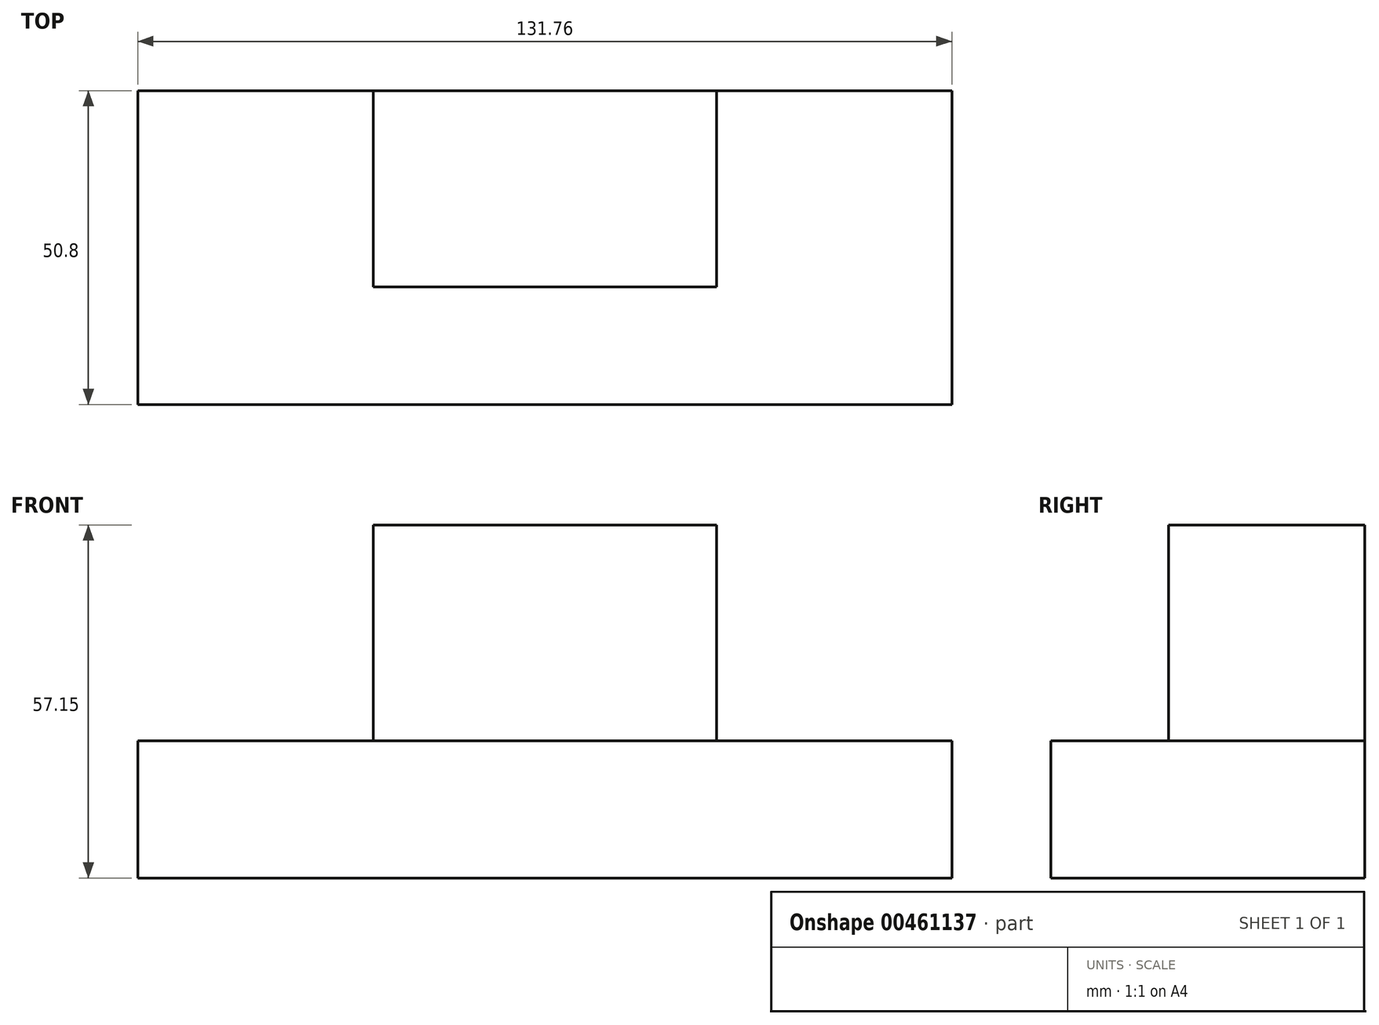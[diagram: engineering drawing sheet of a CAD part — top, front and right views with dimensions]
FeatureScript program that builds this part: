
annotation { "Feature Type Name" : "Feature", "Feature Type Description" : "" }
export const myFeature = defineFeature(function(context is Context, id is Id, definition is map)
    precondition{}
    {
        {
            var Q0;
            Q0=qCreatedBy(makeId("Front.planeOp"),FACE);
            var sketch = newSketch(context, id + "F0", { "sketchPlane" : qUnion([Q0])});
            skLineSegment(sketch, "E0.bottom", {"start": v(0, 0) * mm, "end": v(131.76, 0) * mm});
            skLineSegment(sketch, "E0.top", {"start": v(0, 22.23) * mm, "end": v(131.76, 22.23) * mm});
            skLineSegment(sketch, "E0.left", {"start": v(0, 0) * mm, "end": v(0, 22.23) * mm});
            skLineSegment(sketch, "E0.right", {"start": v(131.76, 0) * mm, "end": v(131.76, 22.23) * mm});
            skSolve(sketch);
        }
        {
            var Q0;
            Q0=makeQuery(id+"F0.imprint","IMPRINT",FACE,{"disambiguationData":[TD([[makeQuery(id+"F0.imprint","IMPRINT",EDGE,{"derivedFrom":sQuery(id+"F0.wireOp",EDGE,"E0.bottom")}),1.0]])]});
            extrude(context, id + "F1", {"entities" : qUnion([Q0]), "oppositeDirection" : true, "depth" : 50.8 * mm});
        }
        {
            var Q0;
            Q0=makeQuery(id+"F1.opExtrude","SWEPT_FACE",FACE,{"disambiguationData":[OSD([sQuery(id+"F0.wireOp",EDGE,"E0.top")])]});
            var sketch = newSketch(context, id + "F2", { "sketchPlane" : qUnion([Q0])});
            skLineSegment(sketch, "E1", {"start": v(0, 50.8) * mm, "end": v(38.1, 50.8) * mm});
            skLineSegment(sketch, "E2", {"start": v(131.76, 50.8) * mm, "end": v(93.65, 50.8) * mm});
            skLineSegment(sketch, "E3.bottom", {"start": v(38.1, 50.8) * mm, "end": v(93.66, 50.8) * mm});
            skLineSegment(sketch, "E3.top", {"start": v(38.1, 19.05) * mm, "end": v(93.66, 19.05) * mm});
            skLineSegment(sketch, "E3.left", {"start": v(38.1, 50.8) * mm, "end": v(38.1, 19.05) * mm});
            skLineSegment(sketch, "E3.right", {"start": v(93.66, 50.8) * mm, "end": v(93.66, 19.05) * mm});
            skSolve(sketch);
        }
        {
            var Q0;
            Q0=makeQuery(id+"F2.imprint","IMPRINT",FACE,{"disambiguationData":[TD([[makeQuery(id+"F2.imprint","IMPRINT",EDGE,{"derivedFrom":sQuery(id+"F2.wireOp",EDGE,"E3.top")}),1.0]])]});
            extrude(context, id + "F3", {"entities" : qUnion([Q0]), "operationType" : NewBodyOperationType.ADD, "depth" : 34.92 * mm});
        }
    });
